# Revit family: LED FRAME 04 LZ6120WW
name_source: partatom
category: Luminarias
units: mm (PartAtom-declared; Revit-internal decimal feet)

## family parameters
Compartido = No
Corte con vacíos al cargar = No
Cota de conector redondo = Diámetro de uso
Origen de luz = Sí
Punto de cálculo de habitación = No
Se basa en plano de trabajo = Sí
Siempre vertical = Sí
Tipo de pieza = Normal

## types (1)
- DWN_LZ6120WW
    Cambio de temperatura de color de luz atenuada = <Ninguno>
    Comentarios de vataje = 90-240V
    Descripción = LUMINARIA TIPO CUADRADA PARA SOBREPONER EN TECHO O PLAFON CON CUERPO DE ALUMINIO ACABADO ANONIZADO, IP 20 USO PARA INTERIORES, CUENTA CON 4 LED TIPO CREE CON UNA POTENCIA TOTAL DE 4W, A UNA TEMPERATURA EN BLANCO CALIDO 3000K CON 250 LUMENES, 0.02mA EN CORRIENTE DE OPERACIÓN, IRC 80, APERTURA A 45 GRADOS EN STOCK, ALIMENTADA A 90-240V.
    Elevación por defecto = 1219 mm
    Fabricante = BRILLANT
    Filtro de color = 16777215
    Longitud de símbolo de origen de luz = 500 mm  [stored 1.64042 ft]
    Lámpara = CREE
    Modelo = LZ6120WW
    Watt per fixture = 4
    Ángulo de campo de foco = 45.00°
    Ángulo de enfoque = 45.00°
    Ángulo de inclinación = 60.00°

note: [stored X ft] marks values corroborated as IEEE doubles in the binary element streams (Revit-internal decimal feet)

## geometry (parser evidence)
native form markers: Blend x2
no freeform markers — native parametric forms only
